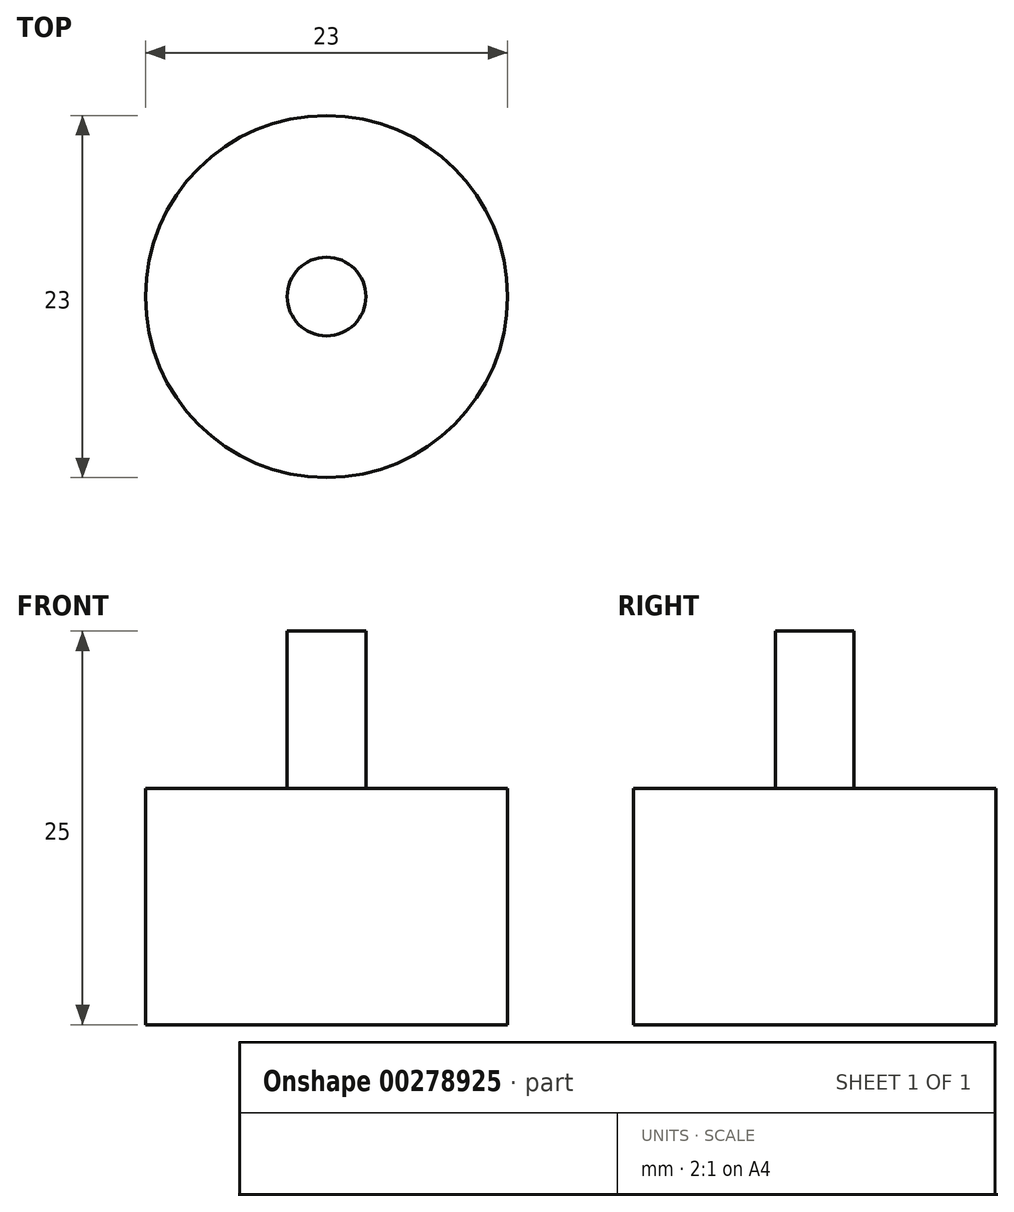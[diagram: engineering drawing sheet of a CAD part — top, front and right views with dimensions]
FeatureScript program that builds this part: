
annotation { "Feature Type Name" : "Feature", "Feature Type Description" : "" }
export const myFeature = defineFeature(function(context is Context, id is Id, definition is map)
    precondition{}
    {
        {
            var Q0;
            Q0=qCreatedBy(makeId("Front.planeOp"),FACE);
            var sketch = newSketch(context, id + "F0", { "sketchPlane" : qUnion([Q0])});
            skLineSegment(sketch, "E0", {"start": v(0, 0) * mm, "end": v(11.5, 0) * mm});
            skLineSegment(sketch, "E1", {"start": v(11.5, 0) * mm, "end": v(11.5, 15) * mm});
            skLineSegment(sketch, "E2", {"start": v(11.5, 15) * mm, "end": v(2.5, 15) * mm});
            skLineSegment(sketch, "E3", {"start": v(2.5, 15) * mm, "end": v(2.5, 25) * mm});
            skLineSegment(sketch, "E4", {"start": v(2.5, 25) * mm, "end": v(0, 25) * mm});
            skLineSegment(sketch, "E5", {"start": v(0, 25) * mm, "end": v(0, 0) * mm});
            skSolve(sketch);
        }
        {
            var Q0;
            Q0=makeQuery(id+"F0.imprint","IMPRINT",FACE,{"disambiguationData":[TD([[makeQuery(id+"F0.imprint","IMPRINT",EDGE,{"derivedFrom":sQuery(id+"F0.wireOp",EDGE,"E0")}),1.0]])]});
            var Q1;
            Q1=sQuery(id+"F0.wireOp",EDGE,"E5");
            revolve(context, id + "F1", {"entities" : qUnion([Q0]), "axis" : qUnion([Q1]), "revolveType" : RevolveType.FULL});
        }
    });
